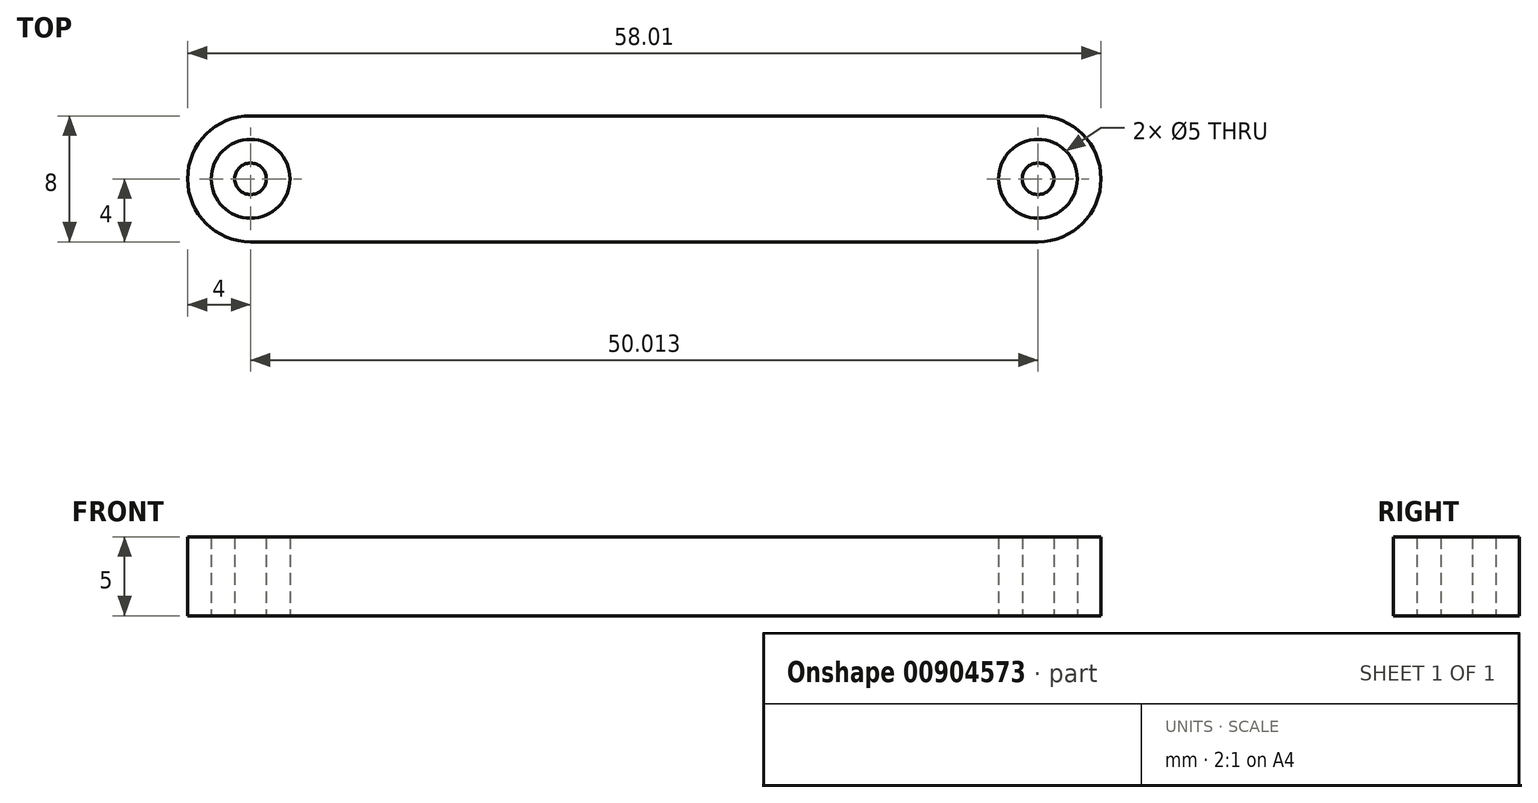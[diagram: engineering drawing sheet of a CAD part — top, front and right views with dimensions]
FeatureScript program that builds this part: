
annotation { "Feature Type Name" : "Feature", "Feature Type Description" : "" }
export const myFeature = defineFeature(function(context is Context, id is Id, definition is map)
    precondition{}
    {
        {
            var Q0;
            Q0=qCreatedBy(makeId("Top.planeOp"),FACE);
            var sketch = newSketch(context, id + "F0", { "sketchPlane" : qUnion([Q0])});
            skCircle(sketch, "E0", {"center": v(0, 0) * mm, "radius": 2.5 * mm});
            skCircle(sketch, "E1", {"center": v(50.01, 0) * mm, "radius": 2.5 * mm});
            skCircle(sketch, "E2", {"center": v(0, 0) * mm, "radius": 1 * mm});
            skCircle(sketch, "E3", {"center": v(50.01, 0) * mm, "radius": 1 * mm});
            skArc(sketch, "E4", {"start": v(0, 4) * mm, "mid": v(-4, 0) * mm, "end": v(0, -4) * mm});
            skArc(sketch, "E5", {"start": v(50.01, -4) * mm, "mid": v(54.01, 0) * mm, "end": v(50.01, 4) * mm});
            skLineSegment(sketch, "E6", {"start": v(0, 4) * mm, "end": v(50.01, 4) * mm});
            skLineSegment(sketch, "E7", {"start": v(0, -4) * mm, "end": v(50.01, -4) * mm});
            skSolve(sketch);
        }
        {
            var Q0;
            Q0 = qSketchRegion(id + "F0", true);
            var Q1;
            Q1=makeQuery(id+"F0.imprint","IMPRINT",FACE,{"disambiguationData":[TD([[makeQuery(id+"F0.imprint","IMPRINT",EDGE,{"derivedFrom":sQuery(id+"F0.wireOp",EDGE,"E2")}),1.0]])]});
            var Q2;
            Q2=makeQuery(id+"F0.imprint","IMPRINT",FACE,{"disambiguationData":[TD([[makeQuery(id+"F0.imprint","IMPRINT",EDGE,{"derivedFrom":sQuery(id+"F0.wireOp",EDGE,"E3")}),1.0]])]});
            extrude(context, id + "F1", {"entities" : qUnion([Q0, Q1, Q2]), "endBound" : BoundingType.SYMMETRIC, "depth" : 5 * mm, "offsetDistance" : 25.4 * mm});
        }
    });
